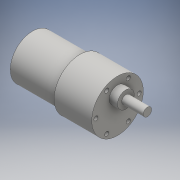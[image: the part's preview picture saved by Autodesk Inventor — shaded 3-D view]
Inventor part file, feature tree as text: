
AUTODESK INVENTOR PART (.ipt)
format: ipt  version: 2016 (Build 200138000, 138)  size: 136,704 bytes
history: native  units: mm
features: extrude x5, sketch x5
ambient origin geometry x8: Origin, YZ Plane, XZ Plane, XY Plane, X Axis, Y Axis, Z Axis, Center Point
bodies: Solid1 (feature_tree)
feature tree (10):
  extrude  "Extrusion1"  Depth=27.0mm TaperAngle=0.0deg
  extrude  "Extrusion2"  Depth=34.0mm TaperAngle=0.0deg
  extrude  "Extrusion3"  Depth=15.5mm
  extrude  "Extrusion4"  Depth=3.0mm TaperAngle=0.0deg
  extrude  "Extrusion5"  Depth=15.5mm
  sketch  "Sketch1"  dims[d0=37.0mm d1=27.0mm d2=0.0mm]
  sketch  "Sketch2"  dims[d3=32.0mm d4=34.0mm d5=0.0mm]
  sketch  "Sketch3"  dims[d8=3.0mm d9=15.5mm]
  sketch  "Sketch4"  dims[d10=60.0mm d12=360.0deg d14=3.0mm d15=0.0mm]
  sketch  "Sketch5"  dims[d16=12.0mm d17=7.0mm d18=6.0mm d19=0.0mm d20=6.0mm d21=7.0mm d22=15.5mm d23=0.0mm]
